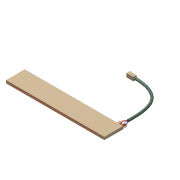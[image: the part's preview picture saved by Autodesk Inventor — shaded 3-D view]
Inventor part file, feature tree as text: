
AUTODESK INVENTOR PART (.ipt)
format: ipt  version: 2015 SP1 (Build 190203100, 203)  size: 428,544 bytes
history: native  units: mm
features: sketch x18, extrude x10, projected_geometry x10, sweep x5, plane x4, fillet x2
ambient origin geometry x8: Origin, YZ Plane, XZ Plane, XY Plane, X Axis, Y Axis, Z Axis, Center Point
bodies: Solid1 (feature_tree)
feature tree (49):
  sketch  "Sketch1"  dims[d0=210.0mm d1=40.0mm]
  extrude  "Extrusion1"  Depth=40.0mm
  extrude  "Extrusion2"  Depth=5.0mm
  extrude  "Extrusion3"  Depth=5.0mm
  extrude  "Extrusion4"  Depth=5.0mm
  extrude  "Extrusion5"  Depth=40.0mm
  extrude  "Extrusion6"  Depth=15.909903mm
  sketch  "Sketch6"  dims[d10=5.0mm d11=15.909903mm]
  plane  "Work Plane1"
  sketch  "Sketch7"  dims[d12=31.819805mm d13=15.909903mm]
  sketch  "Sketch9"  dims[d14=1.0mm d15=0.0mm d16=1.0mm d17=0.0mm]
  sketch  "Sketch10"  dims[d18=1.0mm d19=0.0mm d20=1.0mm d21=0.0mm]
  sketch  "Sketch11"  dims[d22=1.0mm d23=0.0mm d24=1.0mm d25=0.0mm]
  sketch  "Sketch12"  dims[d26=2.0mm d27=2.5mm]
  plane  "Work Plane3"
  plane  "Work Plane4"
  sketch  "Sketch13"  dims[d28=10.0mm d29=5.0mm]
  sketch  "Sketch14"  dims[d30=10.0mm d31=5.0mm]
  plane  "Work Plane5"
  sketch  "Sketch15"  dims[d32=0.8mm d33=0.8mm]
  sweep  "Sweep1"
  sweep  "Sweep2"
  sweep  "Sweep3"
  sweep  "Sweep4"
  sweep  "Sweep5"
  extrude  "Extrusion7"  Depth=5.0mm
  extrude  "Extrusion8"  Depth=5.0mm
  extrude  "Extrusion9"  Depth=0.8mm
  extrude  "Extrusion10"  Depth=0.8mm
  fillet  "Fillet1"  [1 undecoded]
  fillet  "Fillet2"  [1 undecoded]
  sketch  "Sketch2"  dims[d2=8.0mm d3=5.0mm]
  projected_geometry  "Projected Loop1"
  sketch  "Sketch3"  dims[d4=5.0mm d5=5.0mm]
  projected_geometry  "Projected Loop2"
  sketch  "Sketch4"  dims[d6=5.0mm d7=5.0mm]
  projected_geometry  "Projected Loop3"
  projected_geometry  "Projected Loop4"
  projected_geometry  "Projected Loop5"
  sketch  "Sketch5"  dims[d8=40.0mm d9=40.0mm]
  projected_geometry  "Projected Loop6"
  projected_geometry  "Projected Loop7"
  projected_geometry  "Projected Loop8"
  sketch  "Sketch16"  dims[d34=0.8mm d35=0.8mm d36=0.0mm d37=0.0mm d38=0.0mm d39=0.0mm]
  sketch  "Sketch17"  dims[d40=0.0mm d41=0.0mm]
  projected_geometry  "Projected Loop9"
  sketch  "Sketch18"  dims[d42=0.0mm d43=0.0mm]
  sketch  "Sketch19"  dims[d44=0.0mm d45=0.0mm d46=1.0mm d47=1.0mm d48=1.0mm d49=15.0mm d50=12.0mm d51=8.0mm d52=0.0mm d53=4.0mm d54=1.5mm d55=1.5mm d56=1.2mm d57=4.0mm d58=12.0mm d59=0.0mm d60=10.0mm d61=0.0mm d62=10.0mm d63=0.0mm d64=0.2mm d65=0.2mm]
  projected_geometry  "Projected Loop10"
note: 2 required parameter values undecoded (feature->parameter linkage not recoverable at this tier; creation-order binding heuristic only, values carry confidence <= 0.55)
